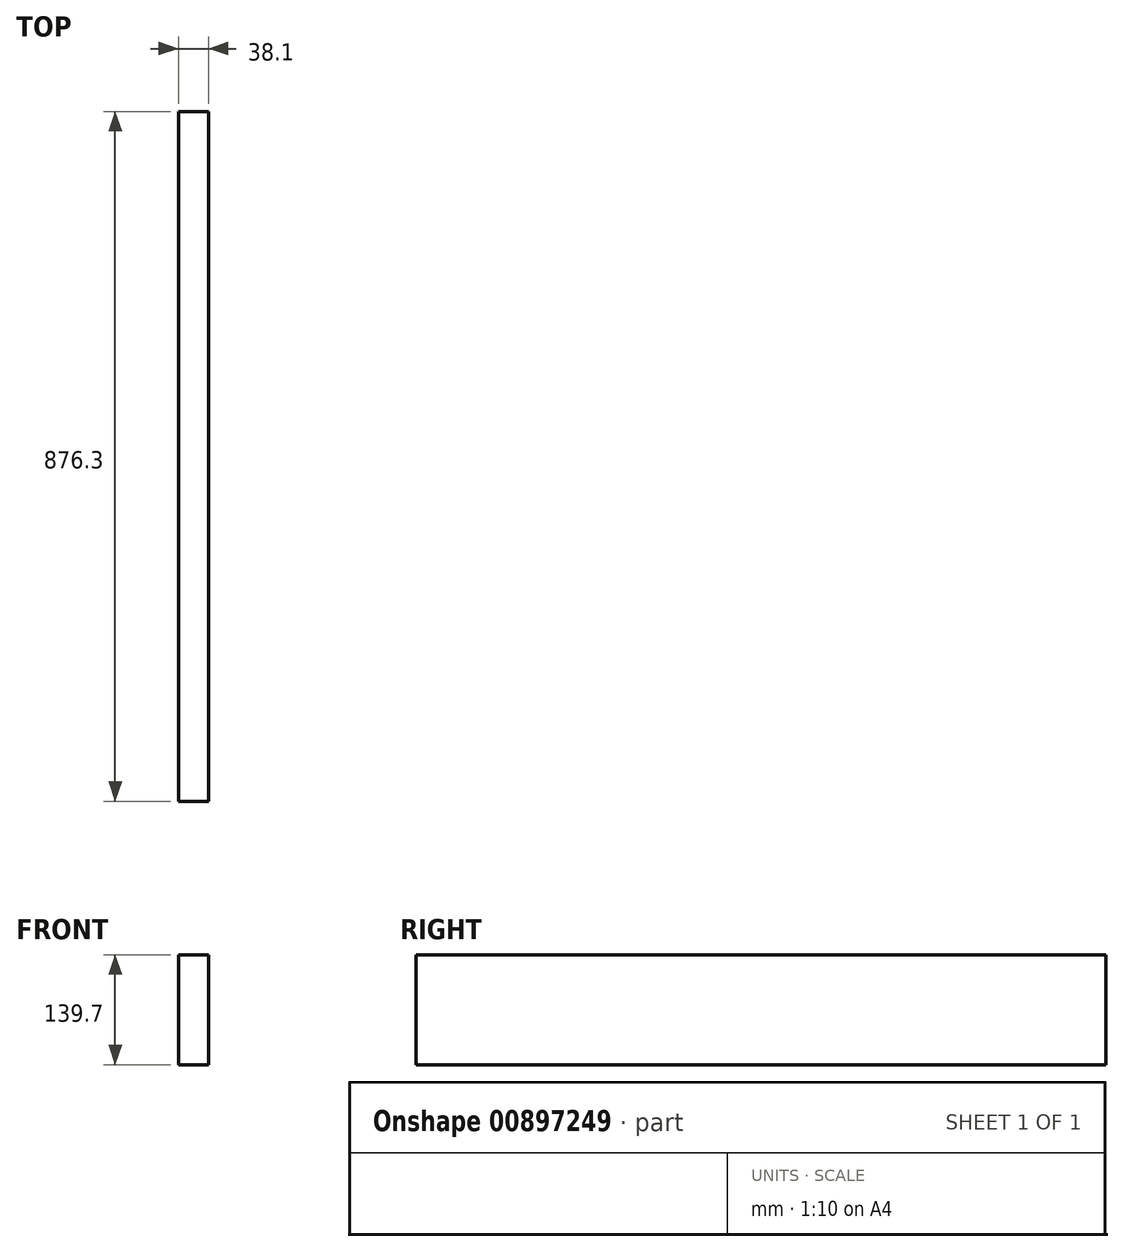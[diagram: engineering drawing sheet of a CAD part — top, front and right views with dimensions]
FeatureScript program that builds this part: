
annotation { "Feature Type Name" : "Feature", "Feature Type Description" : "" }
export const myFeature = defineFeature(function(context is Context, id is Id, definition is map)
    precondition{}
    {
        {
            var Q0;
            Q0=qCreatedBy(makeId("Front.planeOp"),FACE);
            var sketch = newSketch(context, id + "F0", { "sketchPlane" : qUnion([Q0])});
            skLineSegment(sketch, "E0.bottom", {"start": v(-19.05, 69.85) * mm, "end": v(19.05, 69.85) * mm});
            skLineSegment(sketch, "E0.top", {"start": v(-19.05, -69.85) * mm, "end": v(19.05, -69.85) * mm});
            skLineSegment(sketch, "E0.left", {"start": v(-19.05, 69.85) * mm, "end": v(-19.05, -69.85) * mm});
            skLineSegment(sketch, "E0.right", {"start": v(19.05, 69.85) * mm, "end": v(19.05, -69.85) * mm});
            skPoint(sketch, "E0.middle", {"position": v(0, 0) * mm});
            skSolve(sketch);
        }
        {
            var Q0;
            Q0=makeQuery(id+"F0.imprint","IMPRINT",FACE,{"disambiguationData":[TD([[makeQuery(id+"F0.imprint","IMPRINT",EDGE,{"derivedFrom":sQuery(id+"F0.wireOp",EDGE,"E0.bottom")}),-1.0]])]});
            extrude(context, id + "F1", {"entities" : qUnion([Q0]), "depth" : 876.3 * mm, "offsetDistance" : 25.4 * mm});
        }
    });
